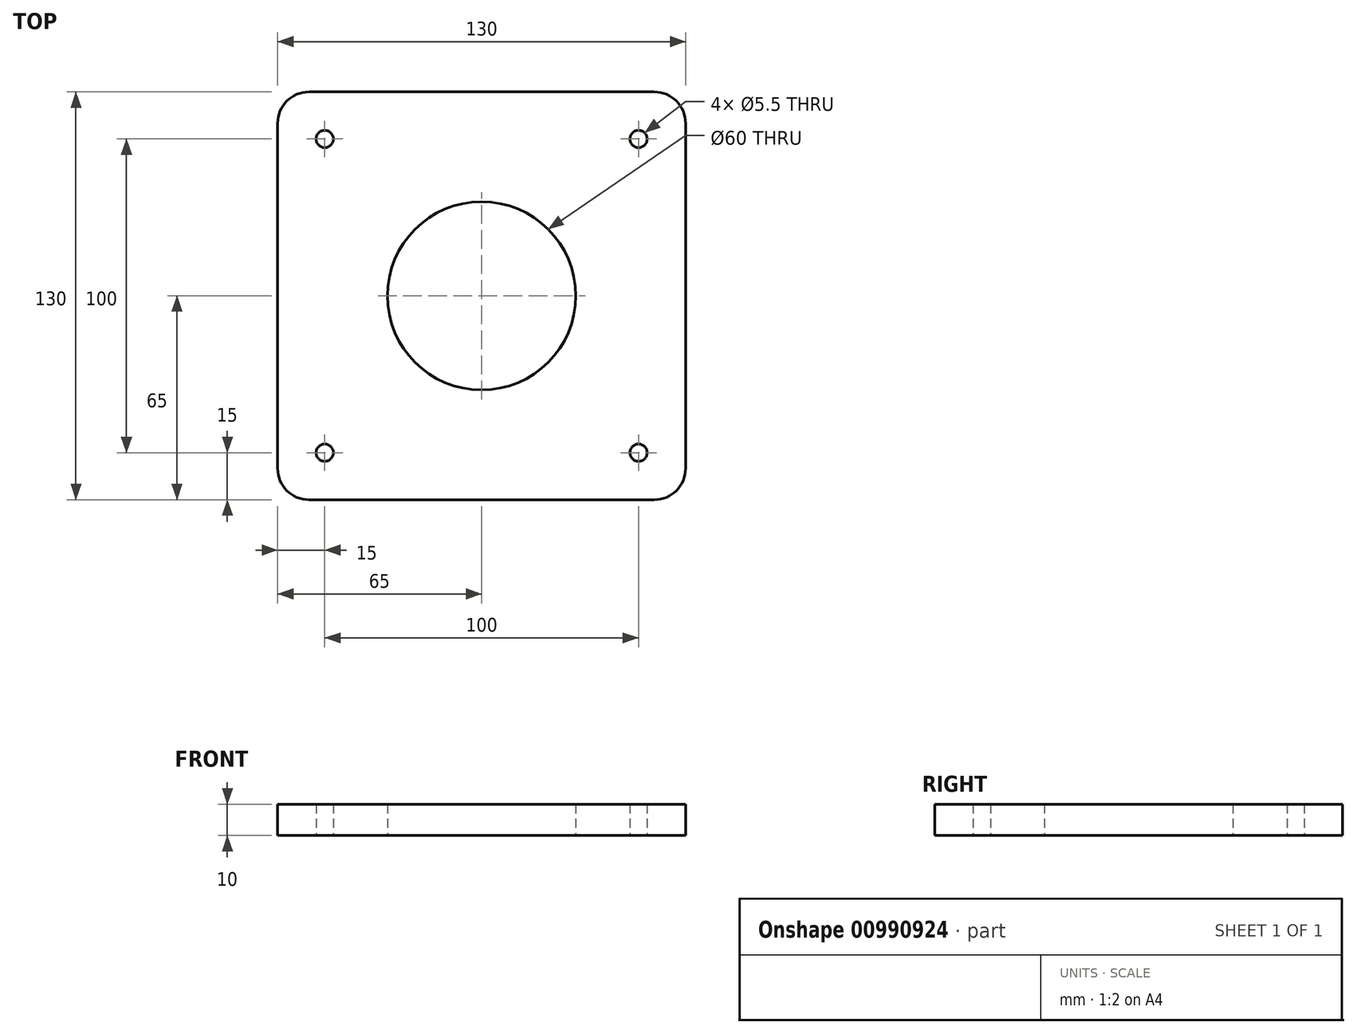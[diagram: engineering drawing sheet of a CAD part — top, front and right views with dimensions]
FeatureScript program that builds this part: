
annotation { "Feature Type Name" : "Feature", "Feature Type Description" : "" }
export const myFeature = defineFeature(function(context is Context, id is Id, definition is map)
    precondition{}
    {
        {
            var Q0;
            Q0=qCreatedBy(makeId("Top.planeOp"),FACE);
            var sketch = newSketch(context, id + "F0", { "sketchPlane" : qUnion([Q0])});
            skLineSegment(sketch, "E0.bottom", {"start": v(55, -65) * mm, "end": v(-55, -65) * mm});
            skLineSegment(sketch, "E0.top", {"start": v(55, 65) * mm, "end": v(-55, 65) * mm});
            skLineSegment(sketch, "E0.left", {"start": v(65, -55) * mm, "end": v(65, 55) * mm});
            skLineSegment(sketch, "E0.right", {"start": v(-65, -55) * mm, "end": v(-65, 55) * mm});
            skPoint(sketch, "E0.middle", {"position": v(0, 0) * mm});
            skCircle(sketch, "E1", {"center": v(0, 0) * mm, "radius": 30 * mm});
            skLineSegment(sketch, "E2", {"start": v(30, 0) * mm, "end": v(65, 0) * mm, "construction": true});
            skLineSegment(sketch, "E3", {"start": v(0, -30) * mm, "end": v(0, -65) * mm, "construction": true});
            skCircle(sketch, "E4", {"center": v(-50, 50) * mm, "radius": 2.75 * mm});
            skCircle(sketch, "E5.MirrorC", {"center": v(50, 50) * mm, "radius": 2.75 * mm});
            skCircle(sketch, "E6.MirrorC", {"center": v(-50, -50) * mm, "radius": 2.75 * mm});
            skCircle(sketch, "E7.MirrorC", {"center": v(50, -50) * mm, "radius": 2.75 * mm});
            skPoint(sketch, "E8.visualSharp", {"position": v(-65, 65) * mm});
            skArc(sketch, "E8.filletArc", {"start": v(-55, 65) * mm, "mid": v(-62.07, 62.07) * mm, "end": v(-65, 55) * mm});
            skPoint(sketch, "E9.visualSharp", {"position": v(65, 65) * mm});
            skArc(sketch, "E9.filletArc", {"start": v(65, 55) * mm, "mid": v(62.07, 62.07) * mm, "end": v(55, 65) * mm});
            skPoint(sketch, "E10.visualSharp", {"position": v(65, -65) * mm});
            skArc(sketch, "E10.filletArc", {"start": v(55, -65) * mm, "mid": v(62.07, -62.07) * mm, "end": v(65, -55) * mm});
            skPoint(sketch, "E11.visualSharp", {"position": v(-65, -65) * mm});
            skArc(sketch, "E11.filletArc", {"start": v(-65, -55) * mm, "mid": v(-62.07, -62.07) * mm, "end": v(-55, -65) * mm});
            skSolve(sketch);
        }
        {
            var Q0;
            Q0 = qSketchRegion(id + "F0", true);
            extrude(context, id + "F1", {"entities" : qUnion([Q0]), "depth" : 10 * mm, "offsetDistance" : 25 * mm});
        }
    });
